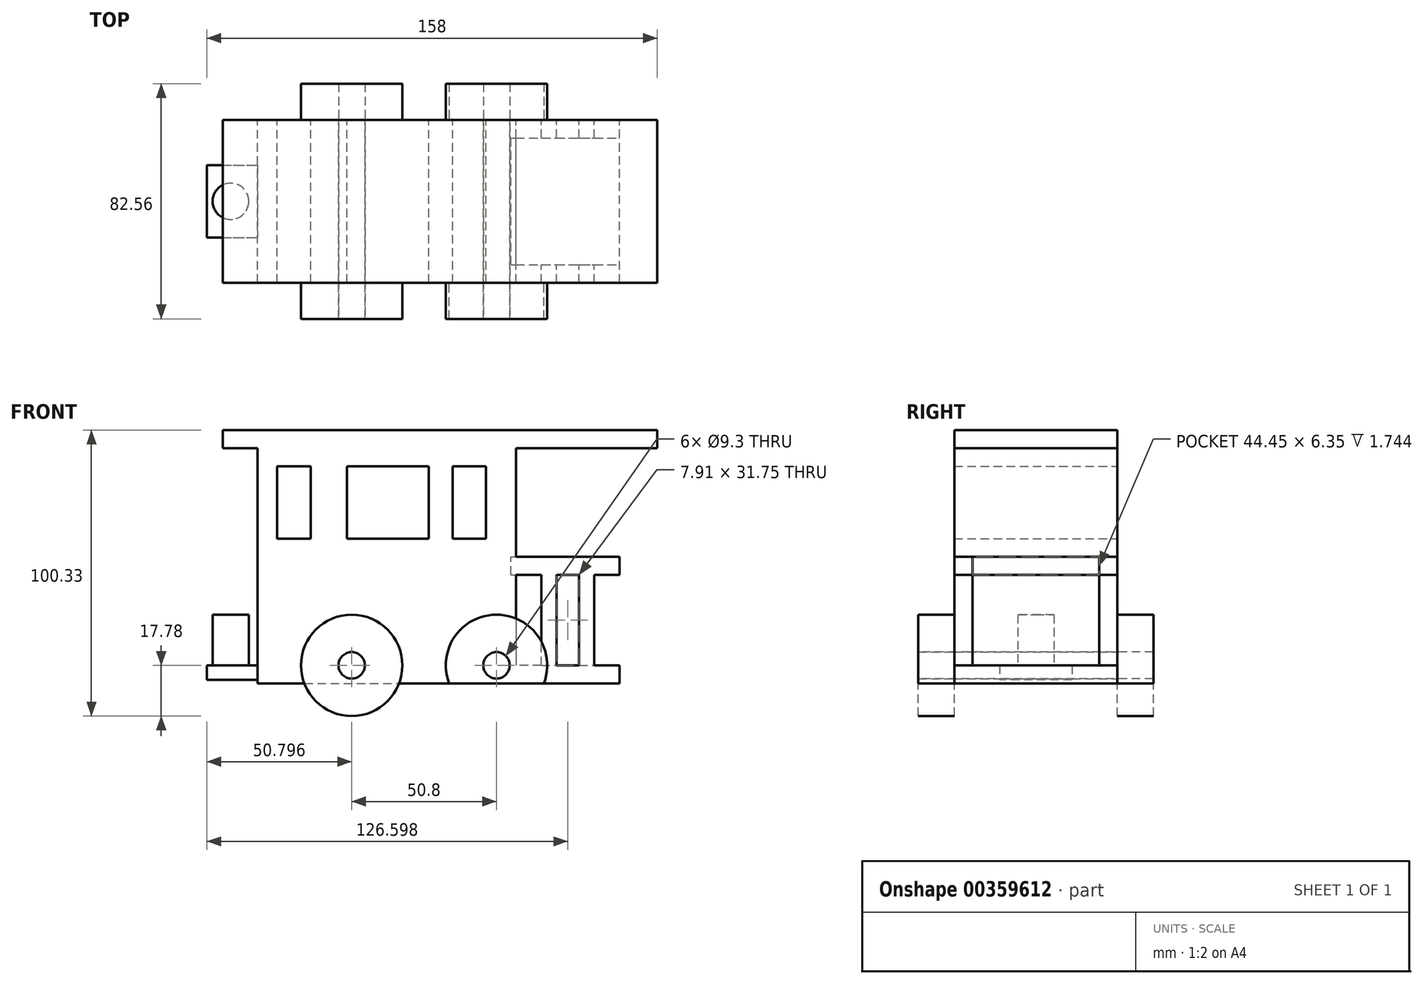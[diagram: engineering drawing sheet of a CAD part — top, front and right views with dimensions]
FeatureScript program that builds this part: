
annotation { "Feature Type Name" : "Feature", "Feature Type Description" : "" }
export const myFeature = defineFeature(function(context is Context, id is Id, definition is map)
    precondition{}
    {
        {
            var Q0;
            Q0=qCreatedBy(makeId("Front.planeOp"),FACE);
            var sketch = newSketch(context, id + "F0", { "sketchPlane" : qUnion([Q0])});
            skLineSegment(sketch, "E0.bottom", {"start": v(-64.27, 50.8) * mm, "end": v(62.73, 50.8) * mm});
            skLineSegment(sketch, "E0.left", {"start": v(-64.27, 50.8) * mm, "end": v(-64.27, -38.1) * mm});
            skLineSegment(sketch, "E0.right", {"start": v(62.73, 50.8) * mm, "end": v(62.73, -38.1) * mm});
            skLineSegment(sketch, "E1.bottom", {"start": v(-57.42, 38.1) * mm, "end": v(-45.6, 38.1) * mm});
            skLineSegment(sketch, "E1.top", {"start": v(-57.42, 12.7) * mm, "end": v(-45.6, 12.7) * mm});
            skLineSegment(sketch, "E1.left", {"start": v(-57.42, 38.1) * mm, "end": v(-57.42, 12.7) * mm});
            skLineSegment(sketch, "E1.right", {"start": v(-45.6, 38.1) * mm, "end": v(-45.6, 12.7) * mm});
            skLineSegment(sketch, "E2.bottom", {"start": v(-32.88, 38.1) * mm, "end": v(-4.19, 38.1) * mm});
            skLineSegment(sketch, "E2.top", {"start": v(-32.88, 12.7) * mm, "end": v(-4.19, 12.7) * mm});
            skLineSegment(sketch, "E2.left", {"start": v(-32.88, 38.1) * mm, "end": v(-32.88, 12.7) * mm});
            skLineSegment(sketch, "E2.right", {"start": v(-4.19, 38.1) * mm, "end": v(-4.19, 12.7) * mm});
            skLineSegment(sketch, "E3.bottom", {"start": v(4.17, 38.1) * mm, "end": v(15.8, 38.1) * mm});
            skLineSegment(sketch, "E3.top", {"start": v(4.17, 12.7) * mm, "end": v(15.8, 12.7) * mm});
            skLineSegment(sketch, "E3.left", {"start": v(4.17, 38.1) * mm, "end": v(4.17, 12.7) * mm});
            skLineSegment(sketch, "E3.right", {"start": v(15.8, 38.1) * mm, "end": v(15.8, 12.7) * mm});
            skLineSegment(sketch, "E4", {"start": v(24.63, 6.35) * mm, "end": v(62.73, 6.35) * mm});
            skLineSegment(sketch, "E5.bottom", {"start": v(-76.45, 50.8) * mm, "end": v(75.95, 50.8) * mm});
            skLineSegment(sketch, "E5.top", {"start": v(-76.45, 44.45) * mm, "end": v(75.95, 44.45) * mm});
            skLineSegment(sketch, "E5.left", {"start": v(-76.45, 50.8) * mm, "end": v(-76.45, 44.45) * mm});
            skLineSegment(sketch, "E5.right", {"start": v(75.95, 50.8) * mm, "end": v(75.95, 44.45) * mm});
            skLineSegment(sketch, "E6", {"start": v(26.37, 0) * mm, "end": v(62.73, 0) * mm});
            skLineSegment(sketch, "E7", {"start": v(35.26, -20.73) * mm, "end": v(35.26, 0) * mm});
            skLineSegment(sketch, "E8", {"start": v(40.6, 0) * mm, "end": v(40.6, -22.85) * mm});
            skLineSegment(sketch, "E9", {"start": v(26.37, -14.71) * mm, "end": v(26.37, 44.45) * mm});
            skLineSegment(sketch, "E10", {"start": v(62.73, -31.75) * mm, "end": v(47.49, -31.75) * mm});
            skLineSegment(sketch, "E11", {"start": v(53.84, 0) * mm, "end": v(53.84, -31.75) * mm});
            skLineSegment(sketch, "E12", {"start": v(48.5, -31.75) * mm, "end": v(48.5, 0) * mm});
            skLineSegment(sketch, "E13", {"start": v(-64.27, -38.1) * mm, "end": v(-47.86, -38.1) * mm});
            skLineSegment(sketch, "E14", {"start": v(62.73, -38.1) * mm, "end": v(46.31, -38.1) * mm});
            skLineSegment(sketch, "E15", {"start": v(-14.65, -38.1) * mm, "end": v(13.1, -38.1) * mm});
            skLineSegment(sketch, "E16", {"start": v(-47.86, -38.1) * mm, "end": v(-14.65, -38.1) * mm});
            skLineSegment(sketch, "E17", {"start": v(13.1, -38.1) * mm, "end": v(46.31, -38.1) * mm});
            skLineSegment(sketch, "E18", {"start": v(26.37, -14.71) * mm, "end": v(26.37, -38.1) * mm});
            skLineSegment(sketch, "E19", {"start": v(48.5, -31.75) * mm, "end": v(26.37, -31.75) * mm});
            skLineSegment(sketch, "E20", {"start": v(35.26, -20.73) * mm, "end": v(35.26, -31.75) * mm});
            skLineSegment(sketch, "E21", {"start": v(40.6, -22.85) * mm, "end": v(40.6, -31.75) * mm});
            skSolve(sketch);
        }
        {
            var Q0;
            {var subQ0=sQuery(id+"F0.wireOp",EDGE,"E7");Q0=makeQuery(id+"F0.imprint","IMPRINT",FACE,{"disambiguationData":[TD([[makeQuery(id+"F0.imprint","IMPRINT",EDGE,{"derivedFrom":subQ0}),-1.0]])]});}
            var Q1;
            {var subQ0=sQuery(id+"F0.wireOp",EDGE,"E11");Q1=makeQuery(id+"F0.imprint","IMPRINT",FACE,{"disambiguationData":[TD([[makeQuery(id+"F0.imprint","IMPRINT",EDGE,{"derivedFrom":subQ0}),-1.0]])]});}
            var Q2;
            {var subQ0=sQuery(id+"F0.wireOp",EDGE,"E7");Q2=makeQuery(id+"F0.imprint","IMPRINT",FACE,{"disambiguationData":[TD([[makeQuery(id+"F0.imprint","IMPRINT",EDGE,{"derivedFrom":subQ0}),-1.0]])]});}
            var Q3;
            {var subQ0=sQuery(id+"F0.wireOp",EDGE,"E11");Q3=makeQuery(id+"F0.imprint","IMPRINT",FACE,{"disambiguationData":[TD([[makeQuery(id+"F0.imprint","IMPRINT",EDGE,{"derivedFrom":subQ0}),-1.0]])]});}
            var Q4;
            {var subQ5=sQuery(id+"F0.wireOp",EDGE,"E5.left");Q4=makeQuery(id+"F0.imprint","IMPRINT",FACE,{"disambiguationData":[TD([[makeQuery(id+"F0.imprint","IMPRINT",EDGE,{"derivedFrom":subQ5}),1.0]])]});}
            var Q5;
            {var subQ5=sQuery(id+"F0.wireOp",EDGE,"E5.right");Q5=makeQuery(id+"F0.imprint","IMPRINT",FACE,{"disambiguationData":[TD([[makeQuery(id+"F0.imprint","IMPRINT",EDGE,{"derivedFrom":subQ5}),-1.0]])]});}
            var Q6;
            {var subQ2=sQuery(id+"F0.wireOp",EDGE,"E0.left");var subQ4=sQuery(id+"F0.wireOp",EDGE,"E5.bottom");var subQ8=makeQuery(id+"F0.imprint","INTERSECT",VERTEX,{"derivedFrom":[subQ2,subQ4]});Q6=makeQuery(id+"F0.imprint","IMPRINT",FACE,{"disambiguationData":[TD([[makeQuery(id+"F0.imprint","IMPRINT",EDGE,{"disambiguationData":[TD([[subQ8,-1.0]])],"derivedFrom":subQ2}),1.0]])]});}
            var Q7;
            {var subQ2=sQuery(id+"F0.wireOp",EDGE,"E0.left");var subQ4=sQuery(id+"F0.wireOp",EDGE,"E5.bottom");var subQ8=makeQuery(id+"F0.imprint","INTERSECT",VERTEX,{"derivedFrom":[subQ2,subQ4]});Q7=makeQuery(id+"F0.imprint","IMPRINT",FACE,{"disambiguationData":[TD([[makeQuery(id+"F0.imprint","IMPRINT",EDGE,{"disambiguationData":[TD([[subQ8,-1.0]])],"derivedFrom":subQ2}),1.0]])]});}
            var Q8;
            Q8=makeQuery(id+"F0.imprint","IMPRINT",FACE,{"disambiguationData":[TD([[makeQuery(id+"F0.imprint","IMPRINT",EDGE,{"derivedFrom":sQuery(id+"F0.wireOp",EDGE,"E1.bottom")}),1.0]])]});
            var Q9;
            {var subQ0=sQuery(id+"F0.wireOp",EDGE,"E7");Q9=makeQuery(id+"F0.imprint","IMPRINT",FACE,{"disambiguationData":[TD([[makeQuery(id+"F0.imprint","IMPRINT",EDGE,{"derivedFrom":subQ0}),-1.0]])]});}
            var Q10;
            {var subQ0=sQuery(id+"F0.wireOp",EDGE,"E11");Q10=makeQuery(id+"F0.imprint","IMPRINT",FACE,{"disambiguationData":[TD([[makeQuery(id+"F0.imprint","IMPRINT",EDGE,{"derivedFrom":subQ0}),-1.0]])]});}
            var Q11;
            {var subQ3=sQuery(id+"F0.wireOp",EDGE,"E4");Q11=makeQuery(id+"F0.imprint","IMPRINT",FACE,{"disambiguationData":[TD([[makeQuery(id+"F0.imprint","IMPRINT",EDGE,{"derivedFrom":subQ3}),-1.0]])]});}
            var Q12;
            {var subQ7=sQuery(id+"F0.wireOp",EDGE,"E14");Q12=makeQuery(id+"F0.imprint","IMPRINT",FACE,{"disambiguationData":[TD([[makeQuery(id+"F0.imprint","IMPRINT",EDGE,{"derivedFrom":subQ7}),-1.0]])]});}
            extrude(context, id + "F1", {"entities" : qUnion([Q0, Q1, Q2, Q3, Q4, Q5, Q6, Q7, Q8, Q9, Q10, Q11, Q12]), "endBound" : BoundingType.SYMMETRIC, "depth" : 57.15 * mm});
        }
        {
            var Q0;
            Q0=makeQuery(id+"F1.opExtrude","SWEPT_FACE",FACE,{"disambiguationData":[OSD([sQuery(id+"F0.wireOp",EDGE,"E11")])]});
            var sketch = newSketch(context, id + "F2", { "sketchPlane" : qUnion([Q0])});
            skLineSegment(sketch, "E22", {"start": v(-22.23, 0) * mm, "end": v(-22.22, -31.75) * mm});
            skLineSegment(sketch, "E23", {"start": v(22.23, 0) * mm, "end": v(22.23, -31.75) * mm});
            skSolve(sketch);
        }
        {
            var Q0;
            Q0 = qSketchRegion(id + "F2", true);
            var Q1;
            {var subQ0=sQuery(id+"F2.wireOp",EDGE,"E22");Q1=makeQuery(id+"F2.imprint","IMPRINT",FACE,{"disambiguationData":[TD([[makeQuery(id+"F2.imprint","IMPRINT",EDGE,{"derivedFrom":subQ0}),1.0]])]});}
            extrude(context, id + "F3", {"entities" : qUnion([Q0, Q1]), "operationType" : NewBodyOperationType.REMOVE, "oppositeDirection" : true, "depth" : 25.4 * mm});
        }
        {
            var Q0;
            {var subQ0=sQuery(id+"F0.wireOp",EDGE,"E0.right");Q0=makeQuery(id+"F1.opExtrude","SWEPT_FACE",FACE,{"disambiguationData":[OSD([subQ0]),TDD([makeQuery(id+"F0.imprint","IMPRINT",EDGE,{"disambiguationData":[TD([[makeQuery(id+"F0.imprint","INTERSECT",VERTEX,{"derivedFrom":[subQ0,sQuery(id+"F0.wireOp",EDGE,"E4")]}),-1.0]])],"derivedFrom":subQ0})])]});}
            var sketch = newSketch(context, id + "F4", { "sketchPlane" : qUnion([Q0])});
            skLineSegment(sketch, "E24", {"start": v(-22.23, 0) * mm, "end": v(-22.23, 6.35) * mm});
            skLineSegment(sketch, "E25", {"start": v(22.23, 0) * mm, "end": v(22.23, 6.35) * mm});
            skSolve(sketch);
        }
        {
            var Q0;
            Q0 = qSketchRegion(id + "F4", true);
            var Q1;
            {var subQ0=sQuery(id+"F4.wireOp",EDGE,"E24");Q1=makeQuery(id+"F4.imprint","IMPRINT",FACE,{"disambiguationData":[TD([[makeQuery(id+"F4.imprint","IMPRINT",EDGE,{"derivedFrom":subQ0}),-1.0]])]});}
            extrude(context, id + "F5", {"entities" : qUnion([Q0, Q1]), "operationType" : NewBodyOperationType.REMOVE, "oppositeDirection" : true, "depth" : 38.1 * mm});
        }
        {
            var Q0;
            Q0=makeQuery(id+"F1.opExtrude","CAP_FACE",FACE,{"disambiguationData":[OSD([sQuery(id+"F0.wireOp",EDGE,"E0.left"),sQuery(id+"F0.wireOp",EDGE,"E0.right"),sQuery(id+"F0.wireOp",EDGE,"E1.bottom"),sQuery(id+"F0.wireOp",EDGE,"E1.top"),sQuery(id+"F0.wireOp",EDGE,"E1.left"),sQuery(id+"F0.wireOp",EDGE,"E1.right"),sQuery(id+"F0.wireOp",EDGE,"E2.bottom"),sQuery(id+"F0.wireOp",EDGE,"E2.top"),sQuery(id+"F0.wireOp",EDGE,"E2.left"),sQuery(id+"F0.wireOp",EDGE,"E2.right"),sQuery(id+"F0.wireOp",EDGE,"E3.bottom"),sQuery(id+"F0.wireOp",EDGE,"E3.top"),sQuery(id+"F0.wireOp",EDGE,"E3.left"),sQuery(id+"F0.wireOp",EDGE,"E3.right"),sQuery(id+"F0.wireOp",EDGE,"E4"),sQuery(id+"F0.wireOp",EDGE,"E5.bottom"),sQuery(id+"F0.wireOp",EDGE,"E5.top"),sQuery(id+"F0.wireOp",EDGE,"E5.left"),sQuery(id+"F0.wireOp",EDGE,"E5.right"),sQuery(id+"F0.wireOp",EDGE,"E6"),sQuery(id+"F0.wireOp",EDGE,"E7"),sQuery(id+"F0.wireOp",EDGE,"E8"),sQuery(id+"F0.wireOp",EDGE,"E9"),sQuery(id+"F0.wireOp",EDGE,"E10"),sQuery(id+"F0.wireOp",EDGE,"E11"),sQuery(id+"F0.wireOp",EDGE,"E12"),sQuery(id+"F0.wireOp",EDGE,"E13"),sQuery(id+"F0.wireOp",EDGE,"E14"),sQuery(id+"F0.wireOp",EDGE,"E15"),sQuery(id+"F0.wireOp",EDGE,"E16"),sQuery(id+"F0.wireOp",EDGE,"E17"),sQuery(id+"F0.wireOp",EDGE,"E18"),sQuery(id+"F0.wireOp",EDGE,"E19"),sQuery(id+"F0.wireOp",EDGE,"E20"),sQuery(id+"F0.wireOp",EDGE,"E21")])],"isStart":false});
            var sketch = newSketch(context, id + "F6", { "sketchPlane" : qUnion([Q0])});
            skCircle(sketch, "E26", {"center": v(19.55, -31.75) * mm, "radius": 4.65 * mm});
            skCircle(sketch, "E27", {"center": v(19.55, -31.75) * mm, "radius": 17.78 * mm});
            skCircle(sketch, "E28", {"center": v(-31.25, -31.75) * mm, "radius": 4.65 * mm});
            skCircle(sketch, "E29", {"center": v(-31.25, -31.75) * mm, "radius": 17.78 * mm});
            skSolve(sketch);
        }
        {
            var Q0;
            {var subQ0=sQuery(id+"F6.wireOp",EDGE,"E29");var subQ1=makeQuery(id+"F1.opExtrude","CAP_EDGE",EDGE,{"disambiguationData":[OSD([sQuery(id+"F0.wireOp",EDGE,"E13"),sQuery(id+"F0.wireOp",EDGE,"E14"),sQuery(id+"F0.wireOp",EDGE,"E15"),sQuery(id+"F0.wireOp",EDGE,"E16"),sQuery(id+"F0.wireOp",EDGE,"E17")])],"isStart":false});var subQ2=makeQuery(id+"F6.imprint","INTERSECT",VERTEX,{"disambiguationData":[OD(0.0)],"derivedFrom":[subQ1,subQ0]});Q0=makeQuery(id+"F6.imprint","IMPRINT",FACE,{"disambiguationData":[TD([[makeQuery(id+"F6.imprint","IMPRINT",EDGE,{"disambiguationData":[TD([[subQ2,-1.0]])],"derivedFrom":subQ0}),1.0]])]});}
            var Q1;
            {var subQ0=sQuery(id+"F6.wireOp",EDGE,"E27");var subQ1=sQuery(id+"F0.wireOp",EDGE,"E21");var subQ2=makeQuery(id+"F1.opExtrude","CAP_EDGE",EDGE,{"disambiguationData":[OSD([sQuery(id+"F0.wireOp",EDGE,"E8"),subQ1])],"isStart":false});var subQ3=makeQuery(id+"F6.imprint","INTERSECT",VERTEX,{"derivedFrom":[subQ2,subQ0]});Q1=makeQuery(id+"F6.imprint","IMPRINT",FACE,{"disambiguationData":[TD([[makeQuery(id+"F6.imprint","IMPRINT",EDGE,{"disambiguationData":[TD([[subQ3,1.0]])],"derivedFrom":subQ0}),1.0]])]});}
            var Q2;
            {var subQ0=sQuery(id+"F6.wireOp",EDGE,"E27");var subQ1=sQuery(id+"F0.wireOp",EDGE,"E20");var subQ2=makeQuery(id+"F1.opExtrude","CAP_EDGE",EDGE,{"disambiguationData":[OSD([sQuery(id+"F0.wireOp",EDGE,"E7"),subQ1])],"isStart":false});var subQ3=makeQuery(id+"F6.imprint","INTERSECT",VERTEX,{"derivedFrom":[subQ2,subQ0]});Q2=makeQuery(id+"F6.imprint","IMPRINT",FACE,{"disambiguationData":[TD([[makeQuery(id+"F6.imprint","IMPRINT",EDGE,{"disambiguationData":[TD([[subQ3,-1.0]])],"derivedFrom":subQ0}),1.0]])]});}
            var Q3;
            {var subQ0=sQuery(id+"F6.wireOp",EDGE,"E27");var subQ3=sQuery(id+"F0.wireOp",EDGE,"E21");var subQ17=makeQuery(id+"F1.opExtrude","CAP_EDGE",EDGE,{"disambiguationData":[OSD([sQuery(id+"F0.wireOp",EDGE,"E8"),subQ3])],"isStart":false});var subQ18=makeQuery(id+"F6.imprint","INTERSECT",VERTEX,{"derivedFrom":[subQ17,subQ0]});Q3=makeQuery(id+"F6.imprint","IMPRINT",FACE,{"disambiguationData":[TD([[makeQuery(id+"F6.imprint","IMPRINT",EDGE,{"disambiguationData":[TD([[subQ18,-1.0]])],"derivedFrom":subQ0}),1.0]])]});}
            var Q4;
            Q4=makeQuery(id+"F6.imprint","IMPRINT",FACE,{"disambiguationData":[TD([[makeQuery(id+"F6.imprint","IMPRINT",EDGE,{"derivedFrom":sQuery(id+"F6.wireOp",EDGE,"E28")}),-1.0]])]});
            var Q5;
            {var subQ0=sQuery(id+"F6.wireOp",EDGE,"E27");var subQ1=makeQuery(id+"F1.opExtrude","CAP_EDGE",EDGE,{"disambiguationData":[OSD([sQuery(id+"F0.wireOp",EDGE,"E13"),sQuery(id+"F0.wireOp",EDGE,"E14"),sQuery(id+"F0.wireOp",EDGE,"E15"),sQuery(id+"F0.wireOp",EDGE,"E16"),sQuery(id+"F0.wireOp",EDGE,"E17")])],"isStart":false});var subQ2=makeQuery(id+"F6.imprint","INTERSECT",VERTEX,{"disambiguationData":[OD(0.0)],"derivedFrom":[subQ1,subQ0]});Q5=makeQuery(id+"F6.imprint","IMPRINT",FACE,{"disambiguationData":[TD([[makeQuery(id+"F6.imprint","IMPRINT",EDGE,{"disambiguationData":[TD([[subQ2,-1.0]])],"derivedFrom":subQ0}),1.0]])]});}
            extrude(context, id + "F7", {"entities" : qUnion([Q0, Q1, Q2, Q3, Q4, Q5]), "depth" : 12.7 * mm});
        }
        {
            var Q0;
            Q0=makeQuery(id+"F7.opExtrude","SWEPT_BODY",BODY,{"disambiguationData":[OSD([sQuery(id+"F6.wireOp",EDGE,"E26"),sQuery(id+"F6.wireOp",EDGE,"E27")])]});
            var Q1;
            Q1=makeQuery(id+"F7.opExtrude","SWEPT_BODY",BODY,{"disambiguationData":[OSD([sQuery(id+"F6.wireOp",EDGE,"E28"),sQuery(id+"F6.wireOp",EDGE,"E29")])]});
            var Q2;
            Q2=qCreatedBy(makeId("Front.planeOp"),FACE);
            mirror(context, id + "F8", {"entities" : qUnion([Q0, Q1]), "mirrorPlane" : qUnion([Q2])});
        }
        {
            var Q0;
            Q0=makeQuery(id+"F6.imprint","IMPRINT",FACE,{"disambiguationData":[TD([[makeQuery(id+"F6.imprint","IMPRINT",EDGE,{"derivedFrom":sQuery(id+"F6.wireOp",EDGE,"E26")}),1.0]])]});
            var Q1;
            Q1=makeQuery(id+"F6.imprint","IMPRINT",FACE,{"disambiguationData":[TD([[makeQuery(id+"F6.imprint","IMPRINT",EDGE,{"derivedFrom":sQuery(id+"F6.wireOp",EDGE,"E28")}),1.0]])]});
            extrude(context, id + "F9", {"entities" : qUnion([Q0, Q1]), "operationType" : NewBodyOperationType.REMOVE, "depth" : 12.7 * mm, "hasSecondDirection" : true, "secondDirectionOppositeDirection" : true, "secondDirectionDepth" : 70.1 * mm});
        }
        {
            var Q0;
            Q0=makeQuery(id+"F1.opExtrude","SWEPT_FACE",FACE,{"disambiguationData":[OSD([sQuery(id+"F0.wireOp",EDGE,"E0.left")])]});
            var sketch = newSketch(context, id + "F10", { "sketchPlane" : qUnion([Q0])});
            skLineSegment(sketch, "E30.bottom", {"start": v(-12.7, -31.78) * mm, "end": v(12.7, -31.78) * mm});
            skLineSegment(sketch, "E30.top", {"start": v(-12.7, -36.86) * mm, "end": v(12.7, -36.86) * mm});
            skLineSegment(sketch, "E30.left", {"start": v(-12.7, -31.78) * mm, "end": v(-12.7, -36.86) * mm});
            skLineSegment(sketch, "E30.right", {"start": v(12.7, -31.78) * mm, "end": v(12.7, -36.86) * mm});
            skSolve(sketch);
        }
        {
            var Q0;
            Q0=makeQuery(id+"F10.imprint","IMPRINT",FACE,{"disambiguationData":[TD([[makeQuery(id+"F10.imprint","IMPRINT",EDGE,{"derivedFrom":sQuery(id+"F10.wireOp",EDGE,"E30.bottom")}),-1.0]])]});
            extrude(context, id + "F11", {"entities" : qUnion([Q0]), "operationType" : NewBodyOperationType.ADD, "depth" : 17.78 * mm});
        }
        {
            var Q0;
            Q0=makeQuery(id+"F11.opExtrude","SWEPT_FACE",FACE,{"disambiguationData":[OSD([sQuery(id+"F10.wireOp",EDGE,"E30.bottom")])]});
            var sketch = newSketch(context, id + "F12", { "sketchPlane" : qUnion([Q0])});
            skCircle(sketch, "E31", {"center": v(-73.7, 0) * mm, "radius": 6.35 * mm});
            skSolve(sketch);
        }
        {
            var Q0;
            Q0=makeQuery(id+"F12.imprint","IMPRINT",FACE,{"disambiguationData":[TD([[makeQuery(id+"F12.imprint","IMPRINT",EDGE,{"derivedFrom":sQuery(id+"F12.wireOp",EDGE,"E31")}),1.0]])]});
            extrude(context, id + "F13", {"entities" : qUnion([Q0]), "operationType" : NewBodyOperationType.ADD, "depth" : 17.78 * mm});
        }
        {
            var Q0;
            Q0=makeQuery(id+"F6.imprint","IMPRINT",FACE,{"disambiguationData":[TD([[makeQuery(id+"F6.imprint","IMPRINT",EDGE,{"derivedFrom":sQuery(id+"F6.wireOp",EDGE,"E28")}),1.0]])]});
            var Q1;
            Q1=makeQuery(id+"F6.imprint","IMPRINT",FACE,{"disambiguationData":[TD([[makeQuery(id+"F6.imprint","IMPRINT",EDGE,{"derivedFrom":sQuery(id+"F6.wireOp",EDGE,"E26")}),1.0]])]});
            var Q2;
            Q2=sQuery(id+"F6.wireOp",EDGE,"E28");
            var Q3;
            Q3=sQuery(id+"F6.wireOp",EDGE,"E26");
            extrude(context, id + "F14", {"entities" : qUnion([Q0, Q1]), "surfaceEntities" : qUnion([Q2, Q3]), "oppositeDirection" : true, "depth" : 69.85 * mm, "hasSecondDirection" : true, "secondDirectionOppositeDirection" : false, "secondDirectionDepth" : 12.7 * mm});
        }
    });
